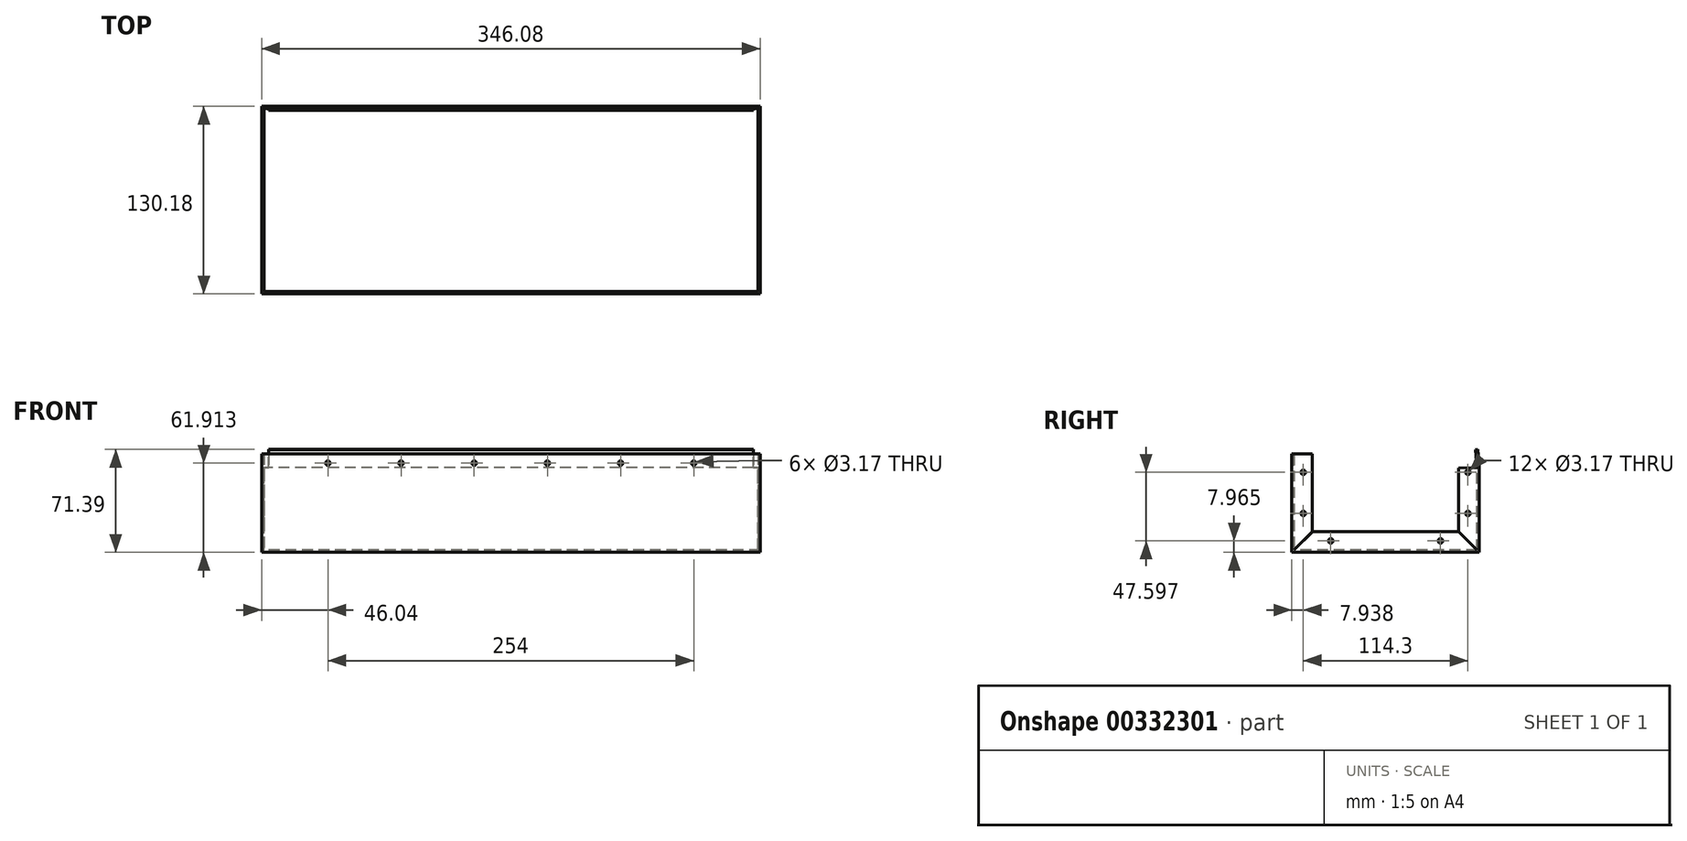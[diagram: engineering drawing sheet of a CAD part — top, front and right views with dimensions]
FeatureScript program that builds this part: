
annotation { "Feature Type Name" : "Feature", "Feature Type Description" : "" }
export const myFeature = defineFeature(function(context is Context, id is Id, definition is map)
    precondition{}
    {
        {
            var Q0;
            Q0=qCreatedBy(makeId("Right.planeOp"),FACE);
            var sketch = newSketch(context, id + "F0", { "sketchPlane" : qUnion([Q0])});
            skLineSegment(sketch, "E0", {"start": v(0, 0) * mm, "end": v(0, 68.26) * mm});
            skLineSegment(sketch, "E1", {"start": v(0, 68.26) * mm, "end": v(1.59, 68.26) * mm});
            skLineSegment(sketch, "E2", {"start": v(1.59, 68.26) * mm, "end": v(1.59, 1.59) * mm});
            skLineSegment(sketch, "E3", {"start": v(1.59, 1.59) * mm, "end": v(128.59, 1.59) * mm});
            skLineSegment(sketch, "E4", {"start": v(128.59, 1.59) * mm, "end": v(128.59, 58.74) * mm});
            skLineSegment(sketch, "E5", {"start": v(130.17, 58.74) * mm, "end": v(130.17, 0) * mm});
            skLineSegment(sketch, "E6", {"start": v(130.17, 0) * mm, "end": v(0, 0) * mm});
            skLineSegment(sketch, "E7", {"start": v(130.17, 58.74) * mm, "end": v(129.07, 71.39) * mm});
            skLineSegment(sketch, "E8", {"start": v(129.07, 71.39) * mm, "end": v(127.49, 71.25) * mm});
            skLineSegment(sketch, "E9", {"start": v(127.49, 71.25) * mm, "end": v(128.59, 58.74) * mm});
            skSolve(sketch);
        }
        {
            var Q0;
            Q0=makeQuery(id+"F0.imprint","IMPRINT",FACE,{"disambiguationData":[TD([[makeQuery(id+"F0.imprint","IMPRINT",EDGE,{"derivedFrom":sQuery(id+"F0.wireOp",EDGE,"E0")}),-1.0]])]});
            extrude(context, id + "F1", {"entities" : qUnion([Q0]), "depth" : 342.9 * mm});
        }
        {
            var Q0;
            Q0=makeQuery(id+"F1.opExtrude","SWEPT_FACE",FACE,{"disambiguationData":[OSD([sQuery(id+"F0.wireOp",EDGE,"E7")])]});
            var sketch = newSketch(context, id + "F2", { "sketchPlane" : qUnion([Q0])});
            skLineSegment(sketch, "E10.bottom", {"start": v(0, 47.17) * mm, "end": v(-3.18, 47.17) * mm});
            skLineSegment(sketch, "E10.top", {"start": v(0, 59.87) * mm, "end": v(-3.18, 59.87) * mm});
            skLineSegment(sketch, "E10.left", {"start": v(0, 47.17) * mm, "end": v(0, 59.87) * mm});
            skLineSegment(sketch, "E10.right", {"start": v(-3.18, 47.17) * mm, "end": v(-3.18, 59.87) * mm});
            skLineSegment(sketch, "E11.bottom", {"start": v(-342.9, 47.17) * mm, "end": v(-339.73, 47.17) * mm});
            skLineSegment(sketch, "E11.top", {"start": v(-342.9, 59.87) * mm, "end": v(-339.73, 59.87) * mm});
            skLineSegment(sketch, "E11.left", {"start": v(-342.9, 47.17) * mm, "end": v(-342.9, 59.87) * mm});
            skLineSegment(sketch, "E11.right", {"start": v(-339.73, 47.17) * mm, "end": v(-339.73, 59.87) * mm});
            skSolve(sketch);
        }
        {
            var Q0;
            Q0=makeQuery(id+"F2.imprint","IMPRINT",FACE,{"disambiguationData":[TD([[makeQuery(id+"F2.imprint","IMPRINT",EDGE,{"derivedFrom":sQuery(id+"F2.wireOp",EDGE,"E11.bottom")}),1.0]])]});
            var Q1;
            Q1=makeQuery(id+"F2.imprint","IMPRINT",FACE,{"disambiguationData":[TD([[makeQuery(id+"F2.imprint","IMPRINT",EDGE,{"derivedFrom":sQuery(id+"F2.wireOp",EDGE,"E10.bottom")}),1.0]])]});
            extrude(context, id + "F3", {"entities" : qUnion([Q0, Q1]), "operationType" : NewBodyOperationType.REMOVE, "endBound" : BoundingType.UP_TO_NEXT, "oppositeDirection" : true, "depth" : 25.4 * mm});
        }
        {
            var Q0;
            Q0=makeQuery(id+"F1.opExtrude","CAP_FACE",FACE,{"disambiguationData":[OSD([sQuery(id+"F0.wireOp",EDGE,"E0"),sQuery(id+"F0.wireOp",EDGE,"E1"),sQuery(id+"F0.wireOp",EDGE,"E2"),sQuery(id+"F0.wireOp",EDGE,"E3"),sQuery(id+"F0.wireOp",EDGE,"E4"),sQuery(id+"F0.wireOp",EDGE,"E5"),sQuery(id+"F0.wireOp",EDGE,"E6"),sQuery(id+"F0.wireOp",EDGE,"E7"),sQuery(id+"F0.wireOp",EDGE,"E8"),sQuery(id+"F0.wireOp",EDGE,"E9")])],"isStart":true});
            var sketch = newSketch(context, id + "F4", { "sketchPlane" : qUnion([Q0])});
            skLineSegment(sketch, "E12", {"start": v(-130.17, 58.74) * mm, "end": v(-115.89, 58.6) * mm});
            skLineSegment(sketch, "E13", {"start": v(-130.17, 0) * mm, "end": v(-115.89, 14.54) * mm});
            skLineSegment(sketch, "E14", {"start": v(-115.89, 58.6) * mm, "end": v(-115.89, 14.54) * mm});
            skLineSegment(sketch, "E15.MirrorCS", {"start": v(-14.29, 58.6) * mm, "end": v(-14.29, 14.54) * mm});
            skLineSegment(sketch, "E16", {"start": v(-130.17, 0) * mm, "end": v(-115.64, 14.29) * mm});
            skLineSegment(sketch, "E17", {"start": v(-130.17, 0) * mm, "end": v(-130.17, 14.29) * mm, "construction": true});
            skLineSegment(sketch, "E18", {"start": v(-115.64, 14.29) * mm, "end": v(-14.54, 14.29) * mm});
            skLineSegment(sketch, "E19", {"start": v(-14.54, 14.29) * mm, "end": v(0, 0) * mm});
            skLineSegment(sketch, "E20", {"start": v(-14.29, 14.54) * mm, "end": v(0, 0) * mm});
            skLineSegment(sketch, "E21", {"start": v(-14.29, 58.6) * mm, "end": v(-14.29, 68.26) * mm});
            skLineSegment(sketch, "E22", {"start": v(-14.29, 68.26) * mm, "end": v(0, 68.26) * mm});
            skSolve(sketch);
        }
        {
            var Q0;
            {var subQ1=sQuery(id+"F0.wireOp",EDGE,"E5");var subQ2=makeQuery(id+"F1.opExtrude","CAP_EDGE",EDGE,{"disambiguationData":[OSD([subQ1])],"isStart":true});Q0=makeQuery(id+"F4.imprint","IMPRINT",FACE,{"disambiguationData":[TD([[makeQuery(id+"F4.imprint","IMPRINT",EDGE,{"derivedFrom":subQ2}),1.0]])]});}
            var Q1;
            Q1=makeQuery(id+"F4.imprint","IMPRINT",FACE,{"disambiguationData":[TD([[makeQuery(id+"F4.imprint","IMPRINT",EDGE,{"derivedFrom":sQuery(id+"F4.wireOp",EDGE,"E12")}),-1.0]])]});
            var Q2;
            {var subQ0=sQuery(id+"F4.wireOp",EDGE,"E18");Q2=makeQuery(id+"F4.imprint","IMPRINT",FACE,{"disambiguationData":[TD([[makeQuery(id+"F4.imprint","IMPRINT",EDGE,{"derivedFrom":subQ0}),-1.0]])]});}
            var Q3;
            {var subQ0=sQuery(id+"F4.wireOp",EDGE,"E15.MirrorCS");Q3=makeQuery(id+"F4.imprint","IMPRINT",FACE,{"disambiguationData":[TD([[makeQuery(id+"F4.imprint","IMPRINT",EDGE,{"derivedFrom":subQ0}),1.0]])]});}
            var Q4;
            {var subQ0=sQuery(id+"F4.wireOp",EDGE,"e9fd83aa-ad33-4bc7-a1fa-165e32fbf3460.MirrorCS");var subQ1=makeQuery(id+"F1.opExtrude","CAP_EDGE",EDGE,{"disambiguationData":[OSD([sQuery(id+"F0.wireOp",EDGE,"E0")])],"isStart":true});var subQ2=makeQuery(id+"F4.imprint","INTERSECT",VERTEX,{"derivedFrom":[subQ1,subQ0]});Q4=makeQuery(id+"F4.imprint","IMPRINT",FACE,{"disambiguationData":[TD([[makeQuery(id+"F4.imprint","IMPRINT",EDGE,{"disambiguationData":[TD([[subQ2,-1.0]])],"derivedFrom":subQ0}),1.0]])]});}
            extrude(context, id + "F5", {"entities" : qUnion([Q0, Q1, Q2, Q3, Q4]), "operationType" : NewBodyOperationType.ADD, "depth" : 1.59 * mm});
        }
        {
            var Q0;
            {var subQ1=sQuery(id+"F0.wireOp",EDGE,"E0");var subQ3=sQuery(id+"F0.wireOp",EDGE,"E5");var subQ4=sQuery(id+"F0.wireOp",EDGE,"E6");var subQ5=sQuery(id+"F0.wireOp",EDGE,"E2");var subQ6=sQuery(id+"F0.wireOp",EDGE,"E3");var subQ7=sQuery(id+"F0.wireOp",EDGE,"E4");Q0=makeQuery(id+"F5.boolean.opBoolean","SPLIT",FACE,{"disambiguationData":[TD([makeQuery(id+"F1.opExtrude","SWEPT_FACE",FACE,{"disambiguationData":[OSD([subQ6])]})])],"derivedFrom":makeQuery(id+"F1.opExtrude","CAP_FACE",FACE,{"disambiguationData":[OSD([subQ1,sQuery(id+"F0.wireOp",EDGE,"E1"),subQ5,subQ6,subQ7,subQ3,subQ4,sQuery(id+"F0.wireOp",EDGE,"E7"),sQuery(id+"F0.wireOp",EDGE,"E8"),sQuery(id+"F0.wireOp",EDGE,"E9")])],"isStart":true})});}
            extrude(context, id + "F6", {"entities" : qUnion([Q0]), "depth" : 1.59 * mm});
        }
        {
            var Q0;
            Q0=makeQuery(id+"F1.opExtrude","SWEPT_BODY",BODY,{"disambiguationData":[OSD([sQuery(id+"F0.wireOp",EDGE,"E0"),sQuery(id+"F0.wireOp",EDGE,"E1"),sQuery(id+"F0.wireOp",EDGE,"E2"),sQuery(id+"F0.wireOp",EDGE,"E3"),sQuery(id+"F0.wireOp",EDGE,"E4"),sQuery(id+"F0.wireOp",EDGE,"E5"),sQuery(id+"F0.wireOp",EDGE,"E6"),sQuery(id+"F0.wireOp",EDGE,"E7"),sQuery(id+"F0.wireOp",EDGE,"E8"),sQuery(id+"F0.wireOp",EDGE,"E9")])]});
            var Q1;
            {var subQ0=sQuery(id+"F0.wireOp",EDGE,"E3");var subQ1=sQuery(id+"F0.wireOp",EDGE,"E0");var subQ2=sQuery(id+"F0.wireOp",EDGE,"E5");Q1=makeQuery(id+"F5.boolean.opBoolean","MERGE",BODY,{"derivedFrom":[makeQuery(id+"F1.opExtrude","SWEPT_BODY",BODY,{"disambiguationData":[OSD([subQ1,sQuery(id+"F0.wireOp",EDGE,"E1"),sQuery(id+"F0.wireOp",EDGE,"E2"),subQ0,sQuery(id+"F0.wireOp",EDGE,"E4"),subQ2,sQuery(id+"F0.wireOp",EDGE,"E6"),sQuery(id+"F0.wireOp",EDGE,"E7"),sQuery(id+"F0.wireOp",EDGE,"E8"),sQuery(id+"F0.wireOp",EDGE,"E9")])]}),makeQuery(id+"F5.opExtrude","SWEPT_BODY",BODY,{"disambiguationData":[OSD([subQ2,sQuery(id+"F4.wireOp",EDGE,"E12"),sQuery(id+"F4.wireOp",EDGE,"E13"),sQuery(id+"F4.wireOp",EDGE,"E14")])]}),makeQuery(id+"F5.opExtrude","SWEPT_BODY",BODY,{"disambiguationData":[OSD([subQ1,sQuery(id+"F4.wireOp",EDGE,"E15.MirrorCS"),sQuery(id+"F4.wireOp",EDGE,"e9fd83aa-ad33-4bc7-a1fa-165e32fbf3460.MirrorCS"),sQuery(id+"F4.wireOp",EDGE,"E20")])]}),makeQuery(id+"F5.opExtrude","SWEPT_BODY",BODY,{"disambiguationData":[OSD([subQ0,sQuery(id+"F4.wireOp",EDGE,"E16"),sQuery(id+"F4.wireOp",EDGE,"E18"),sQuery(id+"F4.wireOp",EDGE,"E19")])]})]});}
            var Q2;
            Q2=makeQuery(id+"F6.opExtrude","SWEPT_BODY",BODY,{"disambiguationData":[OSD([sQuery(id+"F0.wireOp",EDGE,"E0"),sQuery(id+"F0.wireOp",EDGE,"E1"),sQuery(id+"F0.wireOp",EDGE,"E2"),sQuery(id+"F0.wireOp",EDGE,"E3"),sQuery(id+"F0.wireOp",EDGE,"E4"),sQuery(id+"F0.wireOp",EDGE,"E5"),sQuery(id+"F0.wireOp",EDGE,"E6"),sQuery(id+"F0.wireOp",EDGE,"E7"),sQuery(id+"F0.wireOp",EDGE,"E8"),sQuery(id+"F0.wireOp",EDGE,"E9")])]});
            booleanBodies(context, id + "F7", {"operationType" : BooleanOperationType.UNION, "tools" : qUnion([Q0, Q1, Q2])});
        }
        {
            var Q0;
            Q0=makeQuery(id+"F1.opExtrude","CAP_FACE",FACE,{"disambiguationData":[OSD([sQuery(id+"F0.wireOp",EDGE,"E0"),sQuery(id+"F0.wireOp",EDGE,"E1"),sQuery(id+"F0.wireOp",EDGE,"E2"),sQuery(id+"F0.wireOp",EDGE,"E3"),sQuery(id+"F0.wireOp",EDGE,"E4"),sQuery(id+"F0.wireOp",EDGE,"E5"),sQuery(id+"F0.wireOp",EDGE,"E6"),sQuery(id+"F0.wireOp",EDGE,"E7"),sQuery(id+"F0.wireOp",EDGE,"E8"),sQuery(id+"F0.wireOp",EDGE,"E9")])],"isStart":false});
            var sketch = newSketch(context, id + "F8", { "sketchPlane" : qUnion([Q0])});
            skSolve(sketch);
        }
        {
            var Q0;
            Q0=makeQuery(id+"F8.imprint","IMPRINT",FACE,{"disambiguationData":[TD([[makeQuery(id+"F8.imprint","IMPRINT",EDGE,{"derivedFrom":makeQuery(id+"F1.opExtrude","CAP_EDGE",EDGE,{"disambiguationData":[OSD([sQuery(id+"F0.wireOp",EDGE,"E0")])],"isStart":false})}),-1.0]])]});
            var sketch = newSketch(context, id + "F9", { "sketchPlane" : qUnion([Q0])});
            skLineSegment(sketch, "E23", {"start": v(0, 0) * mm, "end": v(14.29, 14.54) * mm});
            skLineSegment(sketch, "E24", {"start": v(14.29, 58.6) * mm, "end": v(14.29, 14.54) * mm});
            skLineSegment(sketch, "E25.MirrorCS", {"start": v(115.89, 58.6) * mm, "end": v(115.89, 14.54) * mm});
            skLineSegment(sketch, "E26.MirrorCS", {"start": v(130.17, 58.74) * mm, "end": v(115.89, 58.6) * mm});
            skLineSegment(sketch, "E27", {"start": v(0, 0) * mm, "end": v(14.54, 14.29) * mm});
            skLineSegment(sketch, "E28", {"start": v(0, 0) * mm, "end": v(0, 14.29) * mm, "construction": true});
            skLineSegment(sketch, "E29", {"start": v(14.54, 14.29) * mm, "end": v(115.64, 14.29) * mm});
            skLineSegment(sketch, "E30", {"start": v(115.64, 14.29) * mm, "end": v(130.17, 0) * mm});
            skLineSegment(sketch, "E31", {"start": v(115.89, 14.54) * mm, "end": v(130.17, 0) * mm});
            skLineSegment(sketch, "E32", {"start": v(0, 0) * mm, "end": v(0, 68.26) * mm, "construction": true});
            skLineSegment(sketch, "E33", {"start": v(0, 68.26) * mm, "end": v(14.29, 68.26) * mm});
            skLineSegment(sketch, "E34", {"start": v(14.29, 68.26) * mm, "end": v(14.29, 58.6) * mm});
            skSolve(sketch);
        }
        {
            var Q0;
            {var subQ0=sQuery(id+"F9.wireOp",EDGE,"E24");Q0=makeQuery(id+"F9.imprint","IMPRINT",FACE,{"disambiguationData":[TD([[makeQuery(id+"F9.imprint","IMPRINT",EDGE,{"derivedFrom":subQ0}),-1.0]])]});}
            var Q1;
            {var subQ0=sQuery(id+"F9.wireOp",EDGE,"de819551-2773-42f9-b412-b950e9d9d3ef");var subQ1=makeQuery(id+"F8.imprint","IMPRINT",EDGE,{"derivedFrom":makeQuery(id+"F1.opExtrude","CAP_EDGE",EDGE,{"disambiguationData":[OSD([sQuery(id+"F0.wireOp",EDGE,"E0")])],"isStart":false})});var subQ2=makeQuery(id+"F9.imprint","INTERSECT",VERTEX,{"derivedFrom":[subQ1,subQ0]});Q1=makeQuery(id+"F9.imprint","IMPRINT",FACE,{"disambiguationData":[TD([[makeQuery(id+"F9.imprint","IMPRINT",EDGE,{"disambiguationData":[TD([[subQ2,-1.0]])],"derivedFrom":subQ0}),-1.0]])]});}
            var Q2;
            {var subQ2=sQuery(id+"F9.wireOp",EDGE,"E25.MirrorCS");Q2=makeQuery(id+"F9.imprint","IMPRINT",FACE,{"disambiguationData":[TD([[makeQuery(id+"F9.imprint","IMPRINT",EDGE,{"derivedFrom":subQ2}),1.0]])]});}
            var Q3;
            {var subQ1=sQuery(id+"F0.wireOp",EDGE,"E5");var subQ2=makeQuery(id+"F8.imprint","IMPRINT",EDGE,{"derivedFrom":makeQuery(id+"F1.opExtrude","CAP_EDGE",EDGE,{"disambiguationData":[OSD([subQ1])],"isStart":false})});Q3=makeQuery(id+"F9.imprint","IMPRINT",FACE,{"disambiguationData":[TD([[makeQuery(id+"F9.imprint","IMPRINT",EDGE,{"derivedFrom":subQ2}),-1.0]])]});}
            var Q4;
            {var subQ0=sQuery(id+"F9.wireOp",EDGE,"E29");Q4=makeQuery(id+"F9.imprint","IMPRINT",FACE,{"disambiguationData":[TD([[makeQuery(id+"F9.imprint","IMPRINT",EDGE,{"derivedFrom":subQ0}),-1.0]])]});}
            var Q5;
            Q5=makeQuery(id+"F8.imprint","IMPRINT",FACE,{"disambiguationData":[TD([[makeQuery(id+"F8.imprint","IMPRINT",EDGE,{"derivedFrom":makeQuery(id+"F1.opExtrude","CAP_EDGE",EDGE,{"disambiguationData":[OSD([sQuery(id+"F0.wireOp",EDGE,"E0")])],"isStart":false})}),-1.0]])]});
            extrude(context, id + "F10", {"entities" : qUnion([Q0, Q1, Q2, Q3, Q4, Q5]), "operationType" : NewBodyOperationType.ADD, "depth" : 1.59 * mm});
        }
        {
            var Q0;
            {var subQ0=sQuery(id+"F0.wireOp",EDGE,"E3");var subQ1=sQuery(id+"F0.wireOp",EDGE,"E2");Q0=makeQuery(id+"F7.opBoolean","MERGE",FACE,{"disambiguationData":[OD(0.0)],"derivedFrom":[makeQuery(id+"F5.opExtrude","CAP_FACE",FACE,{"disambiguationData":[OSD([subQ1,sQuery(id+"F4.wireOp",EDGE,"E15.MirrorCS"),sQuery(id+"F4.wireOp",EDGE,"E20"),sQuery(id+"F4.wireOp",EDGE,"E21"),sQuery(id+"F4.wireOp",EDGE,"E22")])],"isStart":true}),makeQuery(id+"F5.opExtrude","CAP_FACE",FACE,{"disambiguationData":[OSD([subQ0,sQuery(id+"F4.wireOp",EDGE,"E16"),sQuery(id+"F4.wireOp",EDGE,"E18"),sQuery(id+"F4.wireOp",EDGE,"E19")])],"isStart":true}),makeQuery(id+"F6.opExtrude","CAP_FACE",FACE,{"disambiguationData":[OSD([sQuery(id+"F0.wireOp",EDGE,"E0"),sQuery(id+"F0.wireOp",EDGE,"E1"),subQ1,subQ0,sQuery(id+"F0.wireOp",EDGE,"E4"),sQuery(id+"F0.wireOp",EDGE,"E5"),sQuery(id+"F0.wireOp",EDGE,"E6"),sQuery(id+"F0.wireOp",EDGE,"E7"),sQuery(id+"F0.wireOp",EDGE,"E8"),sQuery(id+"F0.wireOp",EDGE,"E9")])],"isStart":true})]});}
            var sketch = newSketch(context, id + "F11", { "sketchPlane" : qUnion([Q0])});
            skLineSegment(sketch, "E35", {"start": v(1.59, 1.62) * mm, "end": v(7.94, 1.62) * mm, "construction": true});
            skLineSegment(sketch, "E36", {"start": v(7.94, 1.62) * mm, "end": v(7.94, 27.02) * mm, "construction": true});
            skLineSegment(sketch, "E37", {"start": v(7.94, 27.02) * mm, "end": v(7.94, 68.26) * mm, "construction": true});
            skLineSegment(sketch, "E38", {"start": v(7.94, 68.26) * mm, "end": v(7.94, 55.56) * mm, "construction": true});
            skLineSegment(sketch, "E39", {"start": v(1.59, 1.62) * mm, "end": v(1.59, 7.97) * mm, "construction": true});
            skLineSegment(sketch, "E40", {"start": v(1.59, 7.97) * mm, "end": v(26.99, 7.97) * mm, "construction": true});
            skLineSegment(sketch, "E41", {"start": v(1.59, 1.62) * mm, "end": v(128.59, 1.62) * mm, "construction": true});
            skPoint(sketch, "E41.endSnap0", {"position": v(4.76, 1.62) * mm});
            skLineSegment(sketch, "E42", {"start": v(65.09, 1.62) * mm, "end": v(65.09, 80.97) * mm, "construction": true});
            skCircle(sketch, "E43", {"center": v(7.94, 55.56) * mm, "radius": 1.59 * mm});
            skCircle(sketch, "E44", {"center": v(7.94, 27.02) * mm, "radius": 1.59 * mm});
            skCircle(sketch, "E45", {"center": v(26.99, 7.97) * mm, "radius": 1.59 * mm});
            skCircle(sketch, "E46.MirrorC", {"center": v(122.24, 55.56) * mm, "radius": 1.59 * mm});
            skCircle(sketch, "E47.MirrorC", {"center": v(122.24, 27.02) * mm, "radius": 1.59 * mm});
            skCircle(sketch, "E48.MirrorC", {"center": v(103.19, 7.97) * mm, "radius": 1.59 * mm});
            skSolve(sketch);
        }
        {
            var Q0;
            Q0=qSketchRegion(id+"F11",true);
            extrude(context, id + "F12", {"entities" : qUnion([Q0]), "operationType" : NewBodyOperationType.REMOVE, "depth" : 889 * mm, "symmetric" : true});
        }
        {
            var Q0;
            {var subQ0=sQuery(id+"F0.wireOp",EDGE,"E0");Q0=makeQuery(id+"F10.boolean.opBoolean","MERGE",FACE,{"derivedFrom":[makeQuery(id+"F7.opBoolean","MERGE",FACE,{"derivedFrom":[makeQuery(id+"F1.opExtrude","SWEPT_FACE",FACE,{"disambiguationData":[OSD([subQ0])]}),makeQuery(id+"F6.opExtrude","SWEPT_FACE",FACE,{"disambiguationData":[OSD([subQ0])]})]}),makeQuery(id+"F10.opExtrude","SWEPT_FACE",FACE,{"disambiguationData":[OSD([subQ0])]})]});}
            var sketch = newSketch(context, id + "F13", { "sketchPlane" : qUnion([Q0])});
            skLineSegment(sketch, "E49", {"start": v(-1.59, 68.26) * mm, "end": v(19.05, 68.26) * mm, "construction": true});
            skLineSegment(sketch, "E50", {"start": v(19.05, 68.26) * mm, "end": v(323.85, 68.26) * mm, "construction": true});
            skLineSegment(sketch, "E51", {"start": v(323.85, 68.26) * mm, "end": v(344.49, 68.26) * mm, "construction": true});
            skLineSegment(sketch, "E52", {"start": v(19.05, 68.26) * mm, "end": v(19.05, 55.56) * mm, "construction": true});
            skLineSegment(sketch, "E53", {"start": v(19.05, 55.56) * mm, "end": v(69.85, 55.56) * mm, "construction": true});
            skLineSegment(sketch, "E54", {"start": v(19.05, 55.56) * mm, "end": v(19.05, 79.02) * mm, "construction": true});
            skPoint(sketch, "E54.endSnap0", {"position": v(19.05, 61.91) * mm});
            skLineSegment(sketch, "E55.0", {"start": v(44.45, 55.56) * mm, "end": v(44.45, 79.02) * mm, "construction": true});
            skLineSegment(sketch, "E56.0", {"start": v(95.25, 55.56) * mm, "end": v(95.25, 79.02) * mm, "construction": true});
            skLineSegment(sketch, "E57.0", {"start": v(146.05, 55.56) * mm, "end": v(146.05, 79.02) * mm, "construction": true});
            skLineSegment(sketch, "E58.0", {"start": v(196.85, 55.56) * mm, "end": v(196.85, 79.02) * mm, "construction": true});
            skLineSegment(sketch, "E59.0", {"start": v(247.65, 55.56) * mm, "end": v(247.65, 79.02) * mm, "construction": true});
            skLineSegment(sketch, "E60.0", {"start": v(298.45, 55.56) * mm, "end": v(298.45, 79.02) * mm, "construction": true});
            skLineSegment(sketch, "E61", {"start": v(19.05, 55.56) * mm, "end": v(19.05, 61.91) * mm, "construction": true});
            skLineSegment(sketch, "E62", {"start": v(19.05, 61.91) * mm, "end": v(337.9, 61.91) * mm, "construction": true});
            skCircle(sketch, "E63", {"center": v(44.45, 61.91) * mm, "radius": 1.59 * mm});
            skCircle(sketch, "E64", {"center": v(95.25, 61.91) * mm, "radius": 1.59 * mm});
            skCircle(sketch, "E65", {"center": v(146.05, 61.91) * mm, "radius": 1.59 * mm});
            skCircle(sketch, "E66", {"center": v(196.85, 61.91) * mm, "radius": 1.59 * mm});
            skCircle(sketch, "E67", {"center": v(247.65, 61.91) * mm, "radius": 1.59 * mm});
            skCircle(sketch, "E68", {"center": v(298.45, 61.91) * mm, "radius": 1.59 * mm});
            skSolve(sketch);
        }
        {
            var Q0;
            Q0=qSketchRegion(id+"F13",true);
            extrude(context, id + "F14", {"entities" : qUnion([Q0]), "operationType" : NewBodyOperationType.REMOVE, "endBound" : BoundingType.UP_TO_NEXT, "oppositeDirection" : true, "depth" : 25.4 * mm});
        }
    });
